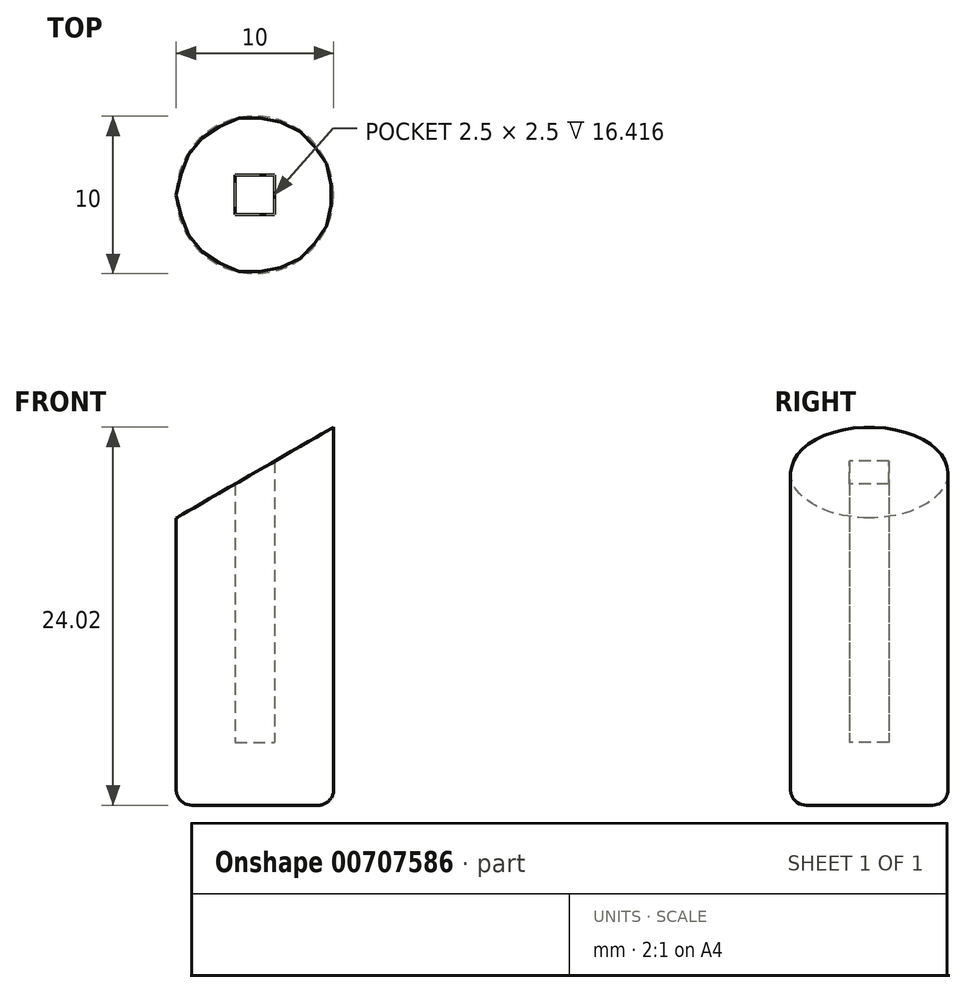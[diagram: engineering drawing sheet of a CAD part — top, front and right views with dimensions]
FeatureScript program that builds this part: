
annotation { "Feature Type Name" : "Feature", "Feature Type Description" : "" }
export const myFeature = defineFeature(function(context is Context, id is Id, definition is map)
    precondition{}
    {
        {
            var Q0;
            Q0=qCreatedBy(makeId("Top.planeOp"),FACE);
            var sketch = newSketch(context, id + "F0", { "sketchPlane" : qUnion([Q0])});
            skLineSegment(sketch, "E0.bottom", {"start": v(-1.25, 1.25) * mm, "end": v(1.25, 1.25) * mm});
            skLineSegment(sketch, "E0.top", {"start": v(-1.25, -1.25) * mm, "end": v(1.25, -1.25) * mm});
            skLineSegment(sketch, "E0.left", {"start": v(-1.25, 1.25) * mm, "end": v(-1.25, -1.25) * mm});
            skLineSegment(sketch, "E0.right", {"start": v(1.25, 1.25) * mm, "end": v(1.25, -1.25) * mm});
            skPoint(sketch, "E0.middle", {"position": v(0, 0) * mm});
            skCircle(sketch, "E1", {"center": v(0, 0) * mm, "radius": 5 * mm});
            skSolve(sketch);
        }
        {
            var Q0;
            Q0=makeQuery(id+"F0.imprint","IMPRINT",FACE,{"disambiguationData":[TD([[makeQuery(id+"F0.imprint","IMPRINT",EDGE,{"derivedFrom":sQuery(id+"F0.wireOp",EDGE,"E0.bottom")}),1.0]])]});
            extrude(context, id + "F1", {"entities" : qUnion([Q0]), "depth" : 25 * mm, "offsetDistance" : 25 * mm});
        }
        {
            var Q0;
            Q0=makeQuery(id+"F0.imprint","IMPRINT",FACE,{"disambiguationData":[TD([[makeQuery(id+"F0.imprint","IMPRINT",EDGE,{"derivedFrom":sQuery(id+"F0.wireOp",EDGE,"E0.bottom")}),-1.0]])]});
            extrude(context, id + "F2", {"entities" : qUnion([Q0]), "operationType" : NewBodyOperationType.ADD, "depth" : 4 * mm, "offsetDistance" : 25 * mm});
        }
        {
            var Q0;
            Q0=makeQuery(id+"F1.opExtrude","CAP_EDGE",EDGE,{"disambiguationData":[OSD([sQuery(id+"F0.wireOp",EDGE,"E1")])],"isStart":true});
            fillet(context, id + "F3", {"entities" : qUnion([Q0]), "radius" : 1 * mm, "tangentPropagation" : true, "allowEdgeOverflow" : false});
        }
        {
            var Q0;
            Q0=qCreatedBy(makeId("Front.planeOp"),FACE);
            var sketch = newSketch(context, id + "F4", { "sketchPlane" : qUnion([Q0])});
            skLineSegment(sketch, "E2", {"start": v(-9.26, 15.79) * mm, "end": v(12.87, 28.57) * mm});
            skLineSegment(sketch, "E3", {"start": v(12.87, 28.57) * mm, "end": v(-3.57, 35.25) * mm});
            skLineSegment(sketch, "E4", {"start": v(-3.57, 35.25) * mm, "end": v(-9.26, 30.2) * mm});
            skLineSegment(sketch, "E5", {"start": v(-9.26, 30.2) * mm, "end": v(-9.26, 15.79) * mm});
            skSolve(sketch);
        }
        {
            var Q0;
            Q0=makeQuery(id+"F4.imprint","IMPRINT",FACE,{"disambiguationData":[TD([[makeQuery(id+"F4.imprint","IMPRINT",EDGE,{"derivedFrom":sQuery(id+"F4.wireOp",EDGE,"E2")}),1.0]])]});
            extrude(context, id + "F5", {"entities" : qUnion([Q0]), "operationType" : NewBodyOperationType.REMOVE, "depth" : 25 * mm, "offsetDistance" : 25 * mm, "hasSecondDirection" : true, "secondDirectionOppositeDirection" : true, "secondDirectionDepth" : 25 * mm});
        }
    });
